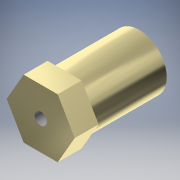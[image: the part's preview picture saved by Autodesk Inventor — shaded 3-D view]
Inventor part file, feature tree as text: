
AUTODESK INVENTOR PART (.ipt)
format: ipt  version: 2016 (Build 200138000, 138)  size: 175,616 bytes
history: native  units: mm
features: sketch x6, extrude x4, hole x2
ambient origin geometry x8: Origin, YZ Plane, XZ Plane, XY Plane, X Axis, Y Axis, Z Axis, Center Point
bodies: Solid1 (feature_tree)
feature tree (12):
  extrude  "Extrusion1"  Depth=4.8mm TaperAngle=0.0deg
  extrude  "Extrusion2"  Depth=3.25mm
  hole  "Hole1"  [1 undecoded]
  hole  "Hole2"  [1 undecoded]
  extrude  "Extrusion8"  Depth=7.621024mm
  extrude  "Extrusion9"  Depth=7.621024mm
  sketch  "Sketch1"  dims[d1=13.65mm d2=4.8mm d3=0.0mm]
  sketch  "Sketch2"  dims[d4=11.0mm d5=3.25mm]
  sketch  "Sketch7"  dims[d7=14.0mm d8=0.0mm d33=3.5mm]
  sketch  "Sketch8"  dims[d34=2.0mm]
  sketch  "Sketch12"  dims[d35=3.2mm d36=6.0mm d37=4.0mm d38=2.0mm d39=90.0deg d40=8.0mm d41=20.594885mm d42=3.0mm]
  sketch  "Sketch14"  dims[d43=2.459mm d44=14.0mm d45=4.0mm d46=2.0mm d47=90.0deg d48=7.0mm d49=20.594885mm d56=2.75mm d64=4.4mm d65=6.0mm d66=0.0mm d67=1.0mm d68=0.0mm d69=7.621024mm]
note: 2 required parameter values undecoded (feature->parameter linkage not recoverable at this tier; creation-order binding heuristic only, values carry confidence <= 0.55)
